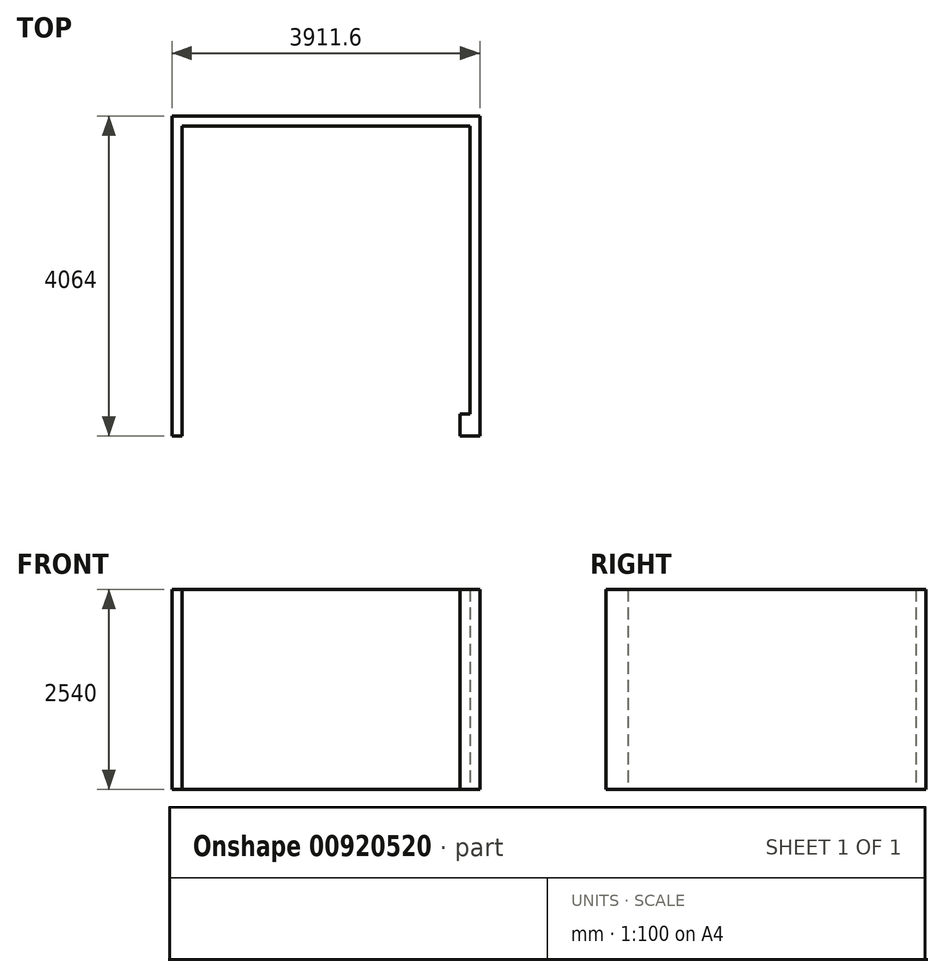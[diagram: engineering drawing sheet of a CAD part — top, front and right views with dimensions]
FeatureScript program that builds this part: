
annotation { "Feature Type Name" : "Feature", "Feature Type Description" : "" }
export const myFeature = defineFeature(function(context is Context, id is Id, definition is map)
    precondition{}
    {
        {
            var Q0;
            Q0=qCreatedBy(makeId("Top.planeOp"),FACE);
            var sketch = newSketch(context, id + "F0", { "sketchPlane" : qUnion([Q0])});
            skLineSegment(sketch, "E0", {"start": v(-1828.8, 0) * mm, "end": v(1828.8, 0) * mm});
            skLineSegment(sketch, "E1", {"start": v(1828.8, 0) * mm, "end": v(1828.8, -3657.6) * mm});
            skLineSegment(sketch, "E2", {"start": v(-1828.8, 0) * mm, "end": v(-1828.8, -3937) * mm});
            skPoint(sketch, "E3", {"position": v(0, 0) * mm});
            skLineSegment(sketch, "E4.0", {"start": v(-1955.8, 127) * mm, "end": v(-1955.8, -3937) * mm});
            skLineSegment(sketch, "E4.1", {"start": v(-1955.8, 127) * mm, "end": v(1955.8, 127) * mm});
            skLineSegment(sketch, "E4.2", {"start": v(1955.8, 127) * mm, "end": v(1955.8, -3937) * mm});
            skLineSegment(sketch, "E5", {"start": v(-1955.8, -3937) * mm, "end": v(-1828.8, -3937) * mm});
            skLineSegment(sketch, "E6", {"start": v(1701.8, -3937) * mm, "end": v(1701.8, -3657.6) * mm});
            skLineSegment(sketch, "E7", {"start": v(1701.8, -3657.6) * mm, "end": v(1828.8, -3657.6) * mm});
            skLineSegment(sketch, "E8", {"start": v(1701.8, -3937) * mm, "end": v(1955.8, -3937) * mm});
            skSolve(sketch);
        }
        {
            var Q0;
            Q0 = qSketchRegion(id + "F0", true);
            extrude(context, id + "F1", {"entities" : qUnion([Q0]), "depth" : 2540 * mm, "offsetDistance" : 25.4 * mm});
        }
    });
